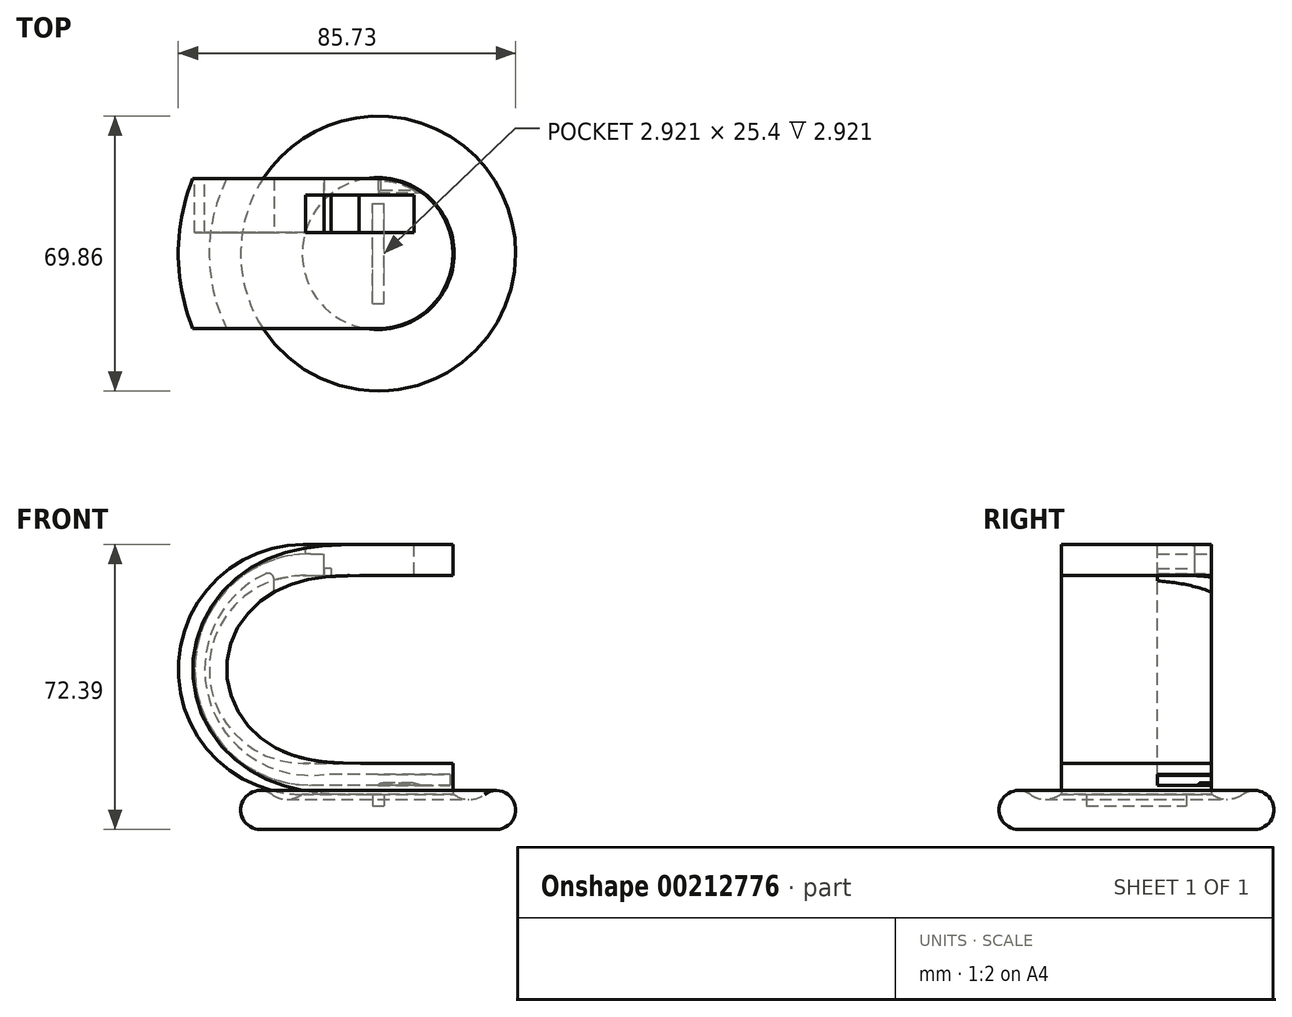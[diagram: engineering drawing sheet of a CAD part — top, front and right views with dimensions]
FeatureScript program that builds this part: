
annotation { "Feature Type Name" : "Feature", "Feature Type Description" : "" }
export const myFeature = defineFeature(function(context is Context, id is Id, definition is map)
    precondition{}
    {
        {
            var Q0;
            Q0=qCreatedBy(makeId("Front.planeOp"),FACE);
            var sketch = newSketch(context, id + "F0", { "sketchPlane" : qUnion([Q0])});
            skLineSegment(sketch, "E0", {"start": v(0, 0) * mm, "end": v(0, 63.5) * mm});
            skLineSegment(sketch, "E1", {"start": v(0, 63.5) * mm, "end": v(-19.05, 63.5) * mm});
            skLineSegment(sketch, "E2", {"start": v(0, 0) * mm, "end": v(-19.05, 0) * mm});
            skArc(sketch, "E3", {"start": v(-19.05, 63.5) * mm, "mid": v(-50.8, 31.75) * mm, "end": v(-19.05, 0) * mm});
            skSolve(sketch);
        }
        {
            var Q0;
            Q0 = qSketchRegion(id + "F0", true);
            var Q1;
            Q1=sQuery(id+"F0.wireOp",EDGE,"E0");
            revolve(context, id + "F22", {"entities" : qUnion([Q0]), "axis" : qUnion([Q1]), "revolveType" : RevolveType.FULL});
        }
        {
            var Q0;
            Q0=qCreatedBy(makeId("Top.planeOp"),FACE);
            var sketch = newSketch(context, id + "F1", { "sketchPlane" : qUnion([Q0])});
            skLineSegment(sketch, "E4", {"start": v(0, 19.05) * mm, "end": v(-51.4, 19.05) * mm});
            skLineSegment(sketch, "E5", {"start": v(0, -19.05) * mm, "end": v(-51.4, -19.05) * mm});
            skArc(sketch, "E6", {"start": v(-51.4, -19.05) * mm, "mid": v(54.82, 0) * mm, "end": v(-51.4, 19.05) * mm});
            skArc(sketch, "E7", {"start": v(0, -19.05) * mm, "mid": v(19.05, 0) * mm, "end": v(0, 19.05) * mm});
            skSolve(sketch);
        }
        {
            var Q0;
            Q0 = qSketchRegion(id + "F1", true);
            extrude(context, id + "F2", {"entities" : qUnion([Q0]), "operationType" : NewBodyOperationType.REMOVE, "endBound" : BoundingType.THROUGH_ALL, "depth" : 25.4 * mm});
        }
        {
            var Q0;
            Q0=qCreatedBy(makeId("Front.planeOp"),FACE);
            var sketch = newSketch(context, id + "F3", { "sketchPlane" : qUnion([Q0])});
            skLineSegment(sketch, "E8", {"start": v(-19.05, 7.87) * mm, "end": v(0, 7.87) * mm});
            skLineSegment(sketch, "E9", {"start": v(0, 7.87) * mm, "end": v(0, 55.63) * mm});
            skLineSegment(sketch, "E10", {"start": v(-19.05, 55.63) * mm, "end": v(0, 55.63) * mm});
            skArc(sketch, "E11", {"start": v(-19.05, 55.63) * mm, "mid": v(-42.93, 31.75) * mm, "end": v(-19.05, 7.87) * mm});
            skSolve(sketch);
        }
        {
            var Q0;
            Q0 = qSketchRegion(id + "F3", true);
            var Q1;
            Q1=sQuery(id+"F3.wireOp",EDGE,"E9");
            revolve(context, id + "F4", {"operationType" : NewBodyOperationType.REMOVE, "entities" : qUnion([Q0]), "axis" : qUnion([Q1]), "revolveType" : RevolveType.FULL, "oppositeDirection" : true});
        }
        {
            var Q0;
            Q0=qCreatedBy(makeId("Right.planeOp"),FACE);
            var sketch = newSketch(context, id + "F23", { "sketchPlane" : qUnion([Q0])});
            skLineSegment(sketch, "E12.bottom", {"start": v(12.7, 0) * mm, "end": v(-12.7, 0) * mm});
            skLineSegment(sketch, "E12.top", {"start": v(5.08, -2.54) * mm, "end": v(-5.08, -2.54) * mm});
            skLineSegment(sketch, "E13", {"start": v(12.7, 0) * mm, "end": v(5.08, -2.54) * mm});
            skLineSegment(sketch, "E14", {"start": v(-12.7, 0) * mm, "end": v(-5.08, -2.54) * mm});
            skSolve(sketch);
        }
        {
            var Q0;
            Q0 = qSketchRegion(id + "F23", true);
            extrude(context, id + "F24", {"entities" : qUnion([Q0]), "operationType" : NewBodyOperationType.ADD, "endBound" : BoundingType.SYMMETRIC, "depth" : 2.54 * mm});
        }
        {
            var Q0;
            Q0=qCreatedBy(makeId("Front.planeOp"),FACE);
            var sketch = newSketch(context, id + "F5", { "sketchPlane" : qUnion([Q0])});
            skLineSegment(sketch, "E15", {"start": v(0, 0) * mm, "end": v(19.3, 0) * mm});
            skLineSegment(sketch, "E16", {"start": v(0, 0) * mm, "end": v(0, -8.9) * mm});
            skLineSegment(sketch, "E17", {"start": v(0, -8.9) * mm, "end": v(29.97, -8.89) * mm});
            skArc(sketch, "E18", {"start": v(19.3, 0) * mm, "mid": v(23.14, -1.3) * mm, "end": v(26.97, 0) * mm});
            skArc(sketch, "E19", {"start": v(29.97, -8.89) * mm, "mid": v(34.66, -2.35) * mm, "end": v(26.97, 0) * mm});
            skSolve(sketch);
        }
        {
            var Q0;
            Q0 = qSketchRegion(id + "F5", true);
            var Q1;
            Q1=sQuery(id+"F5.wireOp",EDGE,"E16");
            revolve(context, id + "F6", {"entities" : qUnion([Q0]), "axis" : qUnion([Q1]), "revolveType" : RevolveType.FULL});
        }
        {
            var Q0;
            Q0=qCreatedBy(makeId("Right.planeOp"),FACE);
            var sketch = newSketch(context, id + "F7", { "sketchPlane" : qUnion([Q0])});
            skLineSegment(sketch, "E20.bottom", {"start": v(-12.7, 0) * mm, "end": v(12.7, 0) * mm});
            skLineSegment(sketch, "E20.top", {"start": v(-12.7, -2.92) * mm, "end": v(12.7, -2.92) * mm});
            skLineSegment(sketch, "E20.left", {"start": v(-12.7, 0) * mm, "end": v(-12.7, -2.92) * mm});
            skLineSegment(sketch, "E20.right", {"start": v(12.7, 0) * mm, "end": v(12.7, -2.92) * mm});
            skSolve(sketch);
        }
        {
            var Q0;
            Q0 = qSketchRegion(id + "F7", true);
            extrude(context, id + "F25", {"entities" : qUnion([Q0]), "operationType" : NewBodyOperationType.REMOVE, "endBound" : BoundingType.SYMMETRIC, "oppositeDirection" : true, "depth" : 2.92 * mm});
        }
        {
            var Q0;
            Q0=makeQuery(id+"F2.boolean.opBoolean","COPY",FACE,{"derivedFrom":makeQuery(id+"F2.opExtrude","SWEPT_FACE",FACE,{"disambiguationData":[OSD([sQuery(id+"F1.wireOp",EDGE,"E4")])]})});
            var sketch = newSketch(context, id + "F8", { "sketchPlane" : qUnion([Q0])});
            skLineSegment(sketch, "E21.bottom", {"start": v(13.78, 55.88) * mm, "end": v(-13.78, 55.88) * mm, "construction": true});
            skLineSegment(sketch, "E21.top", {"start": v(13.78, 63.5) * mm, "end": v(-13.78, 63.5) * mm, "construction": true});
            skLineSegment(sketch, "E21.left", {"start": v(13.78, 55.88) * mm, "end": v(13.78, 63.5) * mm, "construction": true});
            skLineSegment(sketch, "E21.right", {"start": v(-13.78, 55.88) * mm, "end": v(-13.78, 63.5) * mm, "construction": true});
            skPoint(sketch, "E21.middle", {"position": v(0, 59.7) * mm});
            skPoint(sketch, "E22", {"position": v(13.78, 59.69) * mm});
            skArc(sketch, "E23", {"start": v(13.78, 5.08) * mm, "mid": v(44.06, 31.75) * mm, "end": v(13.78, 58.42) * mm});
            skArc(sketch, "E24", {"start": v(17.18, 2.34) * mm, "mid": v(46.58, 31.75) * mm, "end": v(17.18, 61.16) * mm});
            skLineSegment(sketch, "E25", {"start": v(-19.61, 2.34) * mm, "end": v(-19.61, 5.08) * mm});
            skLineSegment(sketch, "E26", {"start": v(-19.61, 5.08) * mm, "end": v(13.78, 5.08) * mm});
            skLineSegment(sketch, "E27", {"start": v(13.78, 58.42) * mm, "end": v(13.78, 60.96) * mm});
            skPoint(sketch, "E28", {"position": v(46.58, 31.75) * mm});
            skPoint(sketch, "E29", {"position": v(47.1, 31.75) * mm});
            skLineSegment(sketch, "E30", {"start": v(17.18, 61.16) * mm, "end": v(13.78, 61.16) * mm});
            skLineSegment(sketch, "E31", {"start": v(13.78, 60.96) * mm, "end": v(13.78, 61.16) * mm});
            skLineSegment(sketch, "E32", {"start": v(-19.61, 2.34) * mm, "end": v(17.18, 2.34) * mm});
            skPoint(sketch, "E33.orphan", {"position": v(13.78, 2.54) * mm});
            skSolve(sketch);
        }
        {
            var Q0;
            Q0 = qSketchRegion(id + "F8", true);
            extrude(context, id + "F9", {"entities" : qUnion([Q0]), "operationType" : NewBodyOperationType.REMOVE, "oppositeDirection" : true, "depth" : 13.72 * mm});
        }
        {
            var Q0;
            Q0=makeQuery(id+"F4.boolean.opBoolean","COPY",FACE,{"derivedFrom":makeQuery(id+"F4.opRevolve","SWEPT_FACE",FACE,{"disambiguationData":[OSD([sQuery(id+"F3.wireOp",EDGE,"E10")])]})});
            var sketch = newSketch(context, id + "F10", { "sketchPlane" : qUnion([Q0])});
            skLineSegment(sketch, "E34.bottom", {"start": v(-13.78, -19.05) * mm, "end": v(-26.48, -19.05) * mm});
            skLineSegment(sketch, "E34.top", {"start": v(-13.78, -5.33) * mm, "end": v(-26.48, -5.33) * mm});
            skLineSegment(sketch, "E34.left", {"start": v(-13.78, -19.05) * mm, "end": v(-13.78, -5.33) * mm});
            skLineSegment(sketch, "E34.right", {"start": v(-26.48, -19.05) * mm, "end": v(-26.48, -5.33) * mm});
            skSolve(sketch);
        }
        {
            var Q0;
            Q0 = qSketchRegion(id + "F10", true);
            extrude(context, id + "F11", {"entities" : qUnion([Q0]), "operationType" : NewBodyOperationType.REMOVE, "depth" : 7.62 * mm});
        }
        {
            var Q0;
            Q0=makeQuery(id+"F11.boolean.opBoolean","MERGE",FACE,{"derivedFrom":[makeQuery(id+"F4.boolean.opBoolean","COPY",FACE,{"derivedFrom":makeQuery(id+"F4.opRevolve","SWEPT_FACE",FACE,{"disambiguationData":[OSD([sQuery(id+"F3.wireOp",EDGE,"E10")])]})}),makeQuery(id+"F11.opExtrude","CAP_FACE",FACE,{"disambiguationData":[OSD([sQuery(id+"F10.wireOp",EDGE,"E34.bottom"),sQuery(id+"F10.wireOp",EDGE,"E34.top"),sQuery(id+"F10.wireOp",EDGE,"E34.left"),sQuery(id+"F10.wireOp",EDGE,"E34.right")])],"isStart":true})]});
            var sketch = newSketch(context, id + "F26", { "sketchPlane" : qUnion([Q0])});
            skLineSegment(sketch, "E35.bottom", {"start": v(-26.48, -5.33) * mm, "end": v(-13.78, -5.33) * mm});
            skLineSegment(sketch, "E35.top", {"start": v(-26.48, -19.05) * mm, "end": v(-13.78, -19.05) * mm});
            skLineSegment(sketch, "E35.left", {"start": v(-26.48, -5.33) * mm, "end": v(-26.48, -19.05) * mm});
            skLineSegment(sketch, "E35.right", {"start": v(-13.78, -5.33) * mm, "end": v(-13.78, -19.05) * mm});
            skSolve(sketch);
        }
        {
            var Q0;
            Q0 = qSketchRegion(id + "F26", true);
            extrude(context, id + "F12", {"entities" : qUnion([Q0]), "operationType" : NewBodyOperationType.REMOVE, "oppositeDirection" : true, "depth" : 3.3 * mm});
        }
        {
            var Q0;
            Q0=makeQuery(id+"F12.boolean.opBoolean","INTERSECT",EDGE,{"derivedFrom":[makeQuery(id+"F9.boolean.opBoolean","COPY",FACE,{"derivedFrom":makeQuery(id+"F9.opExtrude","SWEPT_FACE",FACE,{"disambiguationData":[OSD([sQuery(id+"F8.wireOp",EDGE,"E23")])]})}),makeQuery(id+"F12.opExtrude","SWEPT_FACE",FACE,{"disambiguationData":[OSD([sQuery(id+"F26.wireOp",EDGE,"E35.left")])]})]});
            fillet(context, id + "F13", {"entities" : qUnion([Q0]), "radius" : 1.52 * mm, "tangentPropagation" : true, "allowEdgeOverflow" : false});
        }
        {
            var Q0;
            Q0=makeQuery(id+"F22.opRevolve","SWEPT_FACE",FACE,{"disambiguationData":[OSD([sQuery(id+"F0.wireOp",EDGE,"E1")])]});
            var sketch = newSketch(context, id + "F14", { "sketchPlane" : qUnion([Q0])});
            skLineSegment(sketch, "E36.bottom", {"start": v(-13.78, 5.33) * mm, "end": v(9.08, 5.33) * mm});
            skLineSegment(sketch, "E36.top", {"start": v(-13.78, 14.86) * mm, "end": v(9.08, 14.86) * mm});
            skLineSegment(sketch, "E36.left", {"start": v(-13.78, 5.33) * mm, "end": v(-13.78, 14.86) * mm});
            skLineSegment(sketch, "E36.right", {"start": v(9.08, 5.33) * mm, "end": v(9.08, 14.86) * mm});
            skSolve(sketch);
        }
        {
            var Q0;
            Q0 = qSketchRegion(id + "F14", true);
            extrude(context, id + "F27", {"entities" : qUnion([Q0]), "operationType" : NewBodyOperationType.REMOVE, "oppositeDirection" : true, "depth" : 7.62 * mm});
        }
        {
            var Q0;
            Q0=makeQuery(id+"F27.boolean.opBoolean","COPY",FACE,{"derivedFrom":makeQuery(id+"F27.opExtrude","CAP_FACE",FACE,{"disambiguationData":[OSD([sQuery(id+"F14.wireOp",EDGE,"E36.bottom"),sQuery(id+"F14.wireOp",EDGE,"E36.top"),sQuery(id+"F14.wireOp",EDGE,"E36.left"),sQuery(id+"F14.wireOp",EDGE,"E36.right")])],"isStart":false})});
            var sketch = newSketch(context, id + "F15", { "sketchPlane" : qUnion([Q0])});
            skLineSegment(sketch, "E37.bottom", {"start": v(-13.78, 14.86) * mm, "end": v(-4.89, 14.86) * mm});
            skLineSegment(sketch, "E37.top", {"start": v(-13.78, 5.33) * mm, "end": v(-4.89, 5.33) * mm});
            skLineSegment(sketch, "E37.left", {"start": v(-13.78, 14.86) * mm, "end": v(-13.78, 5.33) * mm});
            skLineSegment(sketch, "E37.right", {"start": v(-4.89, 14.86) * mm, "end": v(-4.89, 5.33) * mm});
            skSolve(sketch);
        }
        {
            var Q0;
            Q0 = qSketchRegion(id + "F15", true);
            extrude(context, id + "F28", {"entities" : qUnion([Q0]), "operationType" : NewBodyOperationType.REMOVE, "oppositeDirection" : true, "depth" : 0.5 * mm});
        }
        {
            var Q0;
            Q0=makeQuery(id+"F28.boolean.opBoolean","MERGE",FACE,{"derivedFrom":[makeQuery(id+"F27.boolean.opBoolean","COPY",FACE,{"derivedFrom":makeQuery(id+"F27.opExtrude","SWEPT_FACE",FACE,{"disambiguationData":[OSD([sQuery(id+"F14.wireOp",EDGE,"E36.top")])]})}),makeQuery(id+"F28.opExtrude","SWEPT_FACE",FACE,{"disambiguationData":[OSD([sQuery(id+"F15.wireOp",EDGE,"E37.bottom")])]})]});
            var sketch = newSketch(context, id + "F29", { "sketchPlane" : qUnion([Q0])});
            skLineSegment(sketch, "E38.bottom", {"start": v(-13.78, 55.6) * mm, "end": v(-11.92, 55.6) * mm});
            skLineSegment(sketch, "E38.top", {"start": v(-13.78, 57.45) * mm, "end": v(-11.92, 57.45) * mm});
            skLineSegment(sketch, "E38.left", {"start": v(-13.78, 55.6) * mm, "end": v(-13.78, 57.45) * mm});
            skLineSegment(sketch, "E38.right", {"start": v(-11.92, 55.6) * mm, "end": v(-11.92, 57.45) * mm});
            skSolve(sketch);
        }
        {
            var Q0;
            Q0 = qSketchRegion(id + "F29", true);
            var Q1;
            Q1=makeQuery(id+"F28.boolean.opBoolean","MERGE",FACE,{"derivedFrom":[makeQuery(id+"F27.boolean.opBoolean","MERGE",FACE,{"derivedFrom":[makeQuery(id+"F12.boolean.opBoolean","MERGE",FACE,{"derivedFrom":[makeQuery(id+"F9.boolean.opBoolean","COPY",FACE,{"derivedFrom":makeQuery(id+"F9.opExtrude","CAP_FACE",FACE,{"disambiguationData":[OSD([sQuery(id+"F8.wireOp",EDGE,"E23"),sQuery(id+"F8.wireOp",EDGE,"E24"),sQuery(id+"F8.wireOp",EDGE,"E25"),sQuery(id+"F8.wireOp",EDGE,"E26"),sQuery(id+"F8.wireOp",EDGE,"E27"),sQuery(id+"F8.wireOp",EDGE,"E30"),sQuery(id+"F8.wireOp",EDGE,"E31"),sQuery(id+"F8.wireOp",EDGE,"E32")])],"isStart":false})}),makeQuery(id+"F11.boolean.opBoolean","COPY",FACE,{"derivedFrom":makeQuery(id+"F11.opExtrude","SWEPT_FACE",FACE,{"disambiguationData":[OSD([sQuery(id+"F10.wireOp",EDGE,"E34.top")])]})}),makeQuery(id+"F12.opExtrude","SWEPT_FACE",FACE,{"disambiguationData":[OSD([sQuery(id+"F26.wireOp",EDGE,"E35.bottom")])]})]}),makeQuery(id+"F27.opExtrude","SWEPT_FACE",FACE,{"disambiguationData":[OSD([sQuery(id+"F14.wireOp",EDGE,"E36.bottom")])]})]}),makeQuery(id+"F28.opExtrude","SWEPT_FACE",FACE,{"disambiguationData":[OSD([sQuery(id+"F15.wireOp",EDGE,"E37.top")])]})]});
            extrude(context, id + "F16", {"entities" : qUnion([Q0]), "operationType" : NewBodyOperationType.ADD, "endBound" : BoundingType.UP_TO_SURFACE, "endBoundEntityFace" : qUnion([Q1]), "depth" : 25.4 * mm});
        }
        {
            var Q0;
            Q0=makeQuery(id+"F22.opRevolve","SWEPT_FACE",FACE,{"disambiguationData":[OSD([sQuery(id+"F0.wireOp",EDGE,"E1")])]});
            var sketch = newSketch(context, id + "F17", { "sketchPlane" : qUnion([Q0])});
            skLineSegment(sketch, "E39.bottom", {"start": v(-13.78, 5.33) * mm, "end": v(-18.48, 5.33) * mm});
            skLineSegment(sketch, "E39.top", {"start": v(-13.78, 14.86) * mm, "end": v(-18.48, 14.86) * mm});
            skLineSegment(sketch, "E39.left", {"start": v(-13.78, 5.33) * mm, "end": v(-13.78, 14.86) * mm});
            skLineSegment(sketch, "E39.right", {"start": v(-18.48, 5.33) * mm, "end": v(-18.48, 14.86) * mm});
            skSolve(sketch);
        }
        {
            var Q0;
            Q0 = qSketchRegion(id + "F17", true);
            extrude(context, id + "F18", {"entities" : qUnion([Q0]), "operationType" : NewBodyOperationType.REMOVE, "oppositeDirection" : true, "depth" : 25.4 * mm});
        }
        {
            var Q0;
            Q0=makeQuery(id+"F9.boolean.opBoolean","COPY",FACE,{"derivedFrom":makeQuery(id+"F9.opExtrude","SWEPT_FACE",FACE,{"disambiguationData":[OSD([sQuery(id+"F8.wireOp",EDGE,"E32")])]})});
            var sketch = newSketch(context, id + "F19", { "sketchPlane" : qUnion([Q0])});
            skArc(sketch, "E40.0", {"start": v(0, 19.05) * mm, "mid": v(11.43, 15.24) * mm, "end": v(18.29, 5.33) * mm});
            skLineSegment(sketch, "E41.top", {"start": v(0, 15.5) * mm, "end": v(11.08, 15.5) * mm});
            skLineSegment(sketch, "E41.left", {"start": v(0, 19.05) * mm, "end": v(0, 15.5) * mm});
            skSolve(sketch);
        }
        {
            var Q0;
            Q0 = qSketchRegion(id + "F19", true);
            extrude(context, id + "F20", {"entities" : qUnion([Q0]), "operationType" : NewBodyOperationType.ADD, "depth" : 0.64 * mm});
        }
        {
            var Q0;
            Q0=makeQuery(id+"F20.opExtrude","CAP_FACE",FACE,{"disambiguationData":[OSD([sQuery(id+"F19.wireOp",EDGE,"E40.0"),sQuery(id+"F19.wireOp",EDGE,"E41.top"),sQuery(id+"F19.wireOp",EDGE,"E41.left")])],"isStart":false});
            chamfer(context, id + "F21", {"entities" : qUnion([Q0]), "width" : 0.64 * mm, "tangentPropagation" : true});
        }
    });
